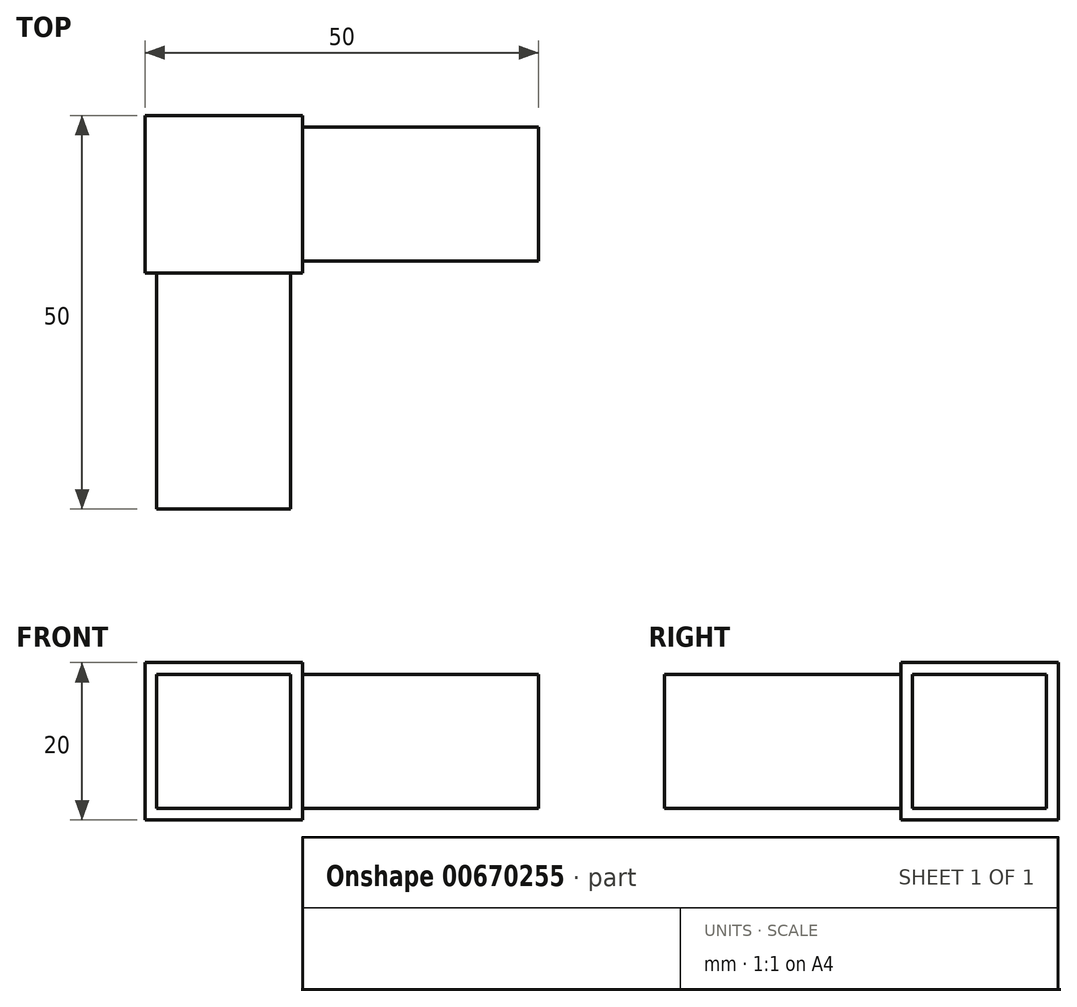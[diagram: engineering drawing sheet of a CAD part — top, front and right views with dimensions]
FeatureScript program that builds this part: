
annotation { "Feature Type Name" : "Feature", "Feature Type Description" : "" }
export const myFeature = defineFeature(function(context is Context, id is Id, definition is map)
    precondition{}
    {
        {
            var Q0;
            Q0=qCreatedBy(makeId("Front.planeOp"),FACE);
            var sketch = newSketch(context, id + "F0", { "sketchPlane" : qUnion([Q0])});
            skLineSegment(sketch, "E0.bottom", {"start": v(-10, -10) * mm, "end": v(10, -10) * mm});
            skLineSegment(sketch, "E0.top", {"start": v(-10, 10) * mm, "end": v(10, 10) * mm});
            skLineSegment(sketch, "E0.left", {"start": v(-10, -10) * mm, "end": v(-10, 10) * mm});
            skLineSegment(sketch, "E0.right", {"start": v(10, -10) * mm, "end": v(10, 10) * mm});
            skSolve(sketch);
        }
        {
            var Q0;
            Q0=qSketchRegion(id+"F0",true);
            extrude(context, id + "F1", {"entities" : qUnion([Q0]), "depth" : 20 * mm, "offsetDistance" : 25 * mm});
        }
        {
            var Q0;
            Q0=makeQuery(id+"F1.opExtrude","SWEPT_BODY",BODY,{"disambiguationData":[OSD([sQuery(id+"F0.wireOp",EDGE,"E0.bottom"),sQuery(id+"F0.wireOp",EDGE,"E0.top"),sQuery(id+"F0.wireOp",EDGE,"E0.left"),sQuery(id+"F0.wireOp",EDGE,"E0.right")])]});
            var Q1;
            Q1=qCreatedBy(makeId("Front.planeOp"),FACE);
            transform(context, id + "F2", {"entities" : qUnion([Q0]), "transformType" : TransformType.TRANSLATION_DISTANCE, "transformDirection" : qUnion([Q1]), "distance" : 10 * mm, "oppositeDirection" : true, "makeCopy" : false});
        }
        {
            var Q0;
            Q0=makeQuery(id+"F1.opExtrude","CAP_FACE",FACE,{"disambiguationData":[OSD([sQuery(id+"F0.wireOp",EDGE,"E0.bottom"),sQuery(id+"F0.wireOp",EDGE,"E0.top"),sQuery(id+"F0.wireOp",EDGE,"E0.left"),sQuery(id+"F0.wireOp",EDGE,"E0.right")])],"isStart":false});
            var sketch = newSketch(context, id + "F3", { "sketchPlane" : qUnion([Q0])});
            skLineSegment(sketch, "E1.bottom", {"start": v(-8.5, 8.5) * mm, "end": v(8.5, 8.5) * mm});
            skLineSegment(sketch, "E1.top", {"start": v(-8.5, -8.5) * mm, "end": v(8.5, -8.5) * mm});
            skLineSegment(sketch, "E1.left", {"start": v(-8.5, 8.5) * mm, "end": v(-8.5, -8.5) * mm});
            skLineSegment(sketch, "E1.right", {"start": v(8.5, 8.5) * mm, "end": v(8.5, -8.5) * mm});
            skSolve(sketch);
        }
        {
            var Q0;
            Q0=qSketchRegion(id+"F3",true);
            extrude(context, id + "F4", {"entities" : qUnion([Q0]), "operationType" : NewBodyOperationType.ADD, "depth" : 30 * mm, "offsetDistance" : 25 * mm});
        }
        {
            var Q0;
            Q0=makeQuery(id+"F1.opExtrude","SWEPT_FACE",FACE,{"disambiguationData":[OSD([sQuery(id+"F0.wireOp",EDGE,"E0.right")])]});
            var sketch = newSketch(context, id + "F5", { "sketchPlane" : qUnion([Q0])});
            skLineSegment(sketch, "E2.bottom", {"start": v(-8.5, 8.5) * mm, "end": v(8.5, 8.5) * mm});
            skLineSegment(sketch, "E2.top", {"start": v(-8.5, -8.5) * mm, "end": v(8.5, -8.5) * mm});
            skLineSegment(sketch, "E2.left", {"start": v(-8.5, 8.5) * mm, "end": v(-8.5, -8.5) * mm});
            skLineSegment(sketch, "E2.right", {"start": v(8.5, 8.5) * mm, "end": v(8.5, -8.5) * mm});
            skSolve(sketch);
        }
        {
            var Q0;
            Q0=qSketchRegion(id+"F5",true);
            extrude(context, id + "F6", {"entities" : qUnion([Q0]), "operationType" : NewBodyOperationType.ADD, "depth" : 30 * mm, "offsetDistance" : 25 * mm});
        }
    });
